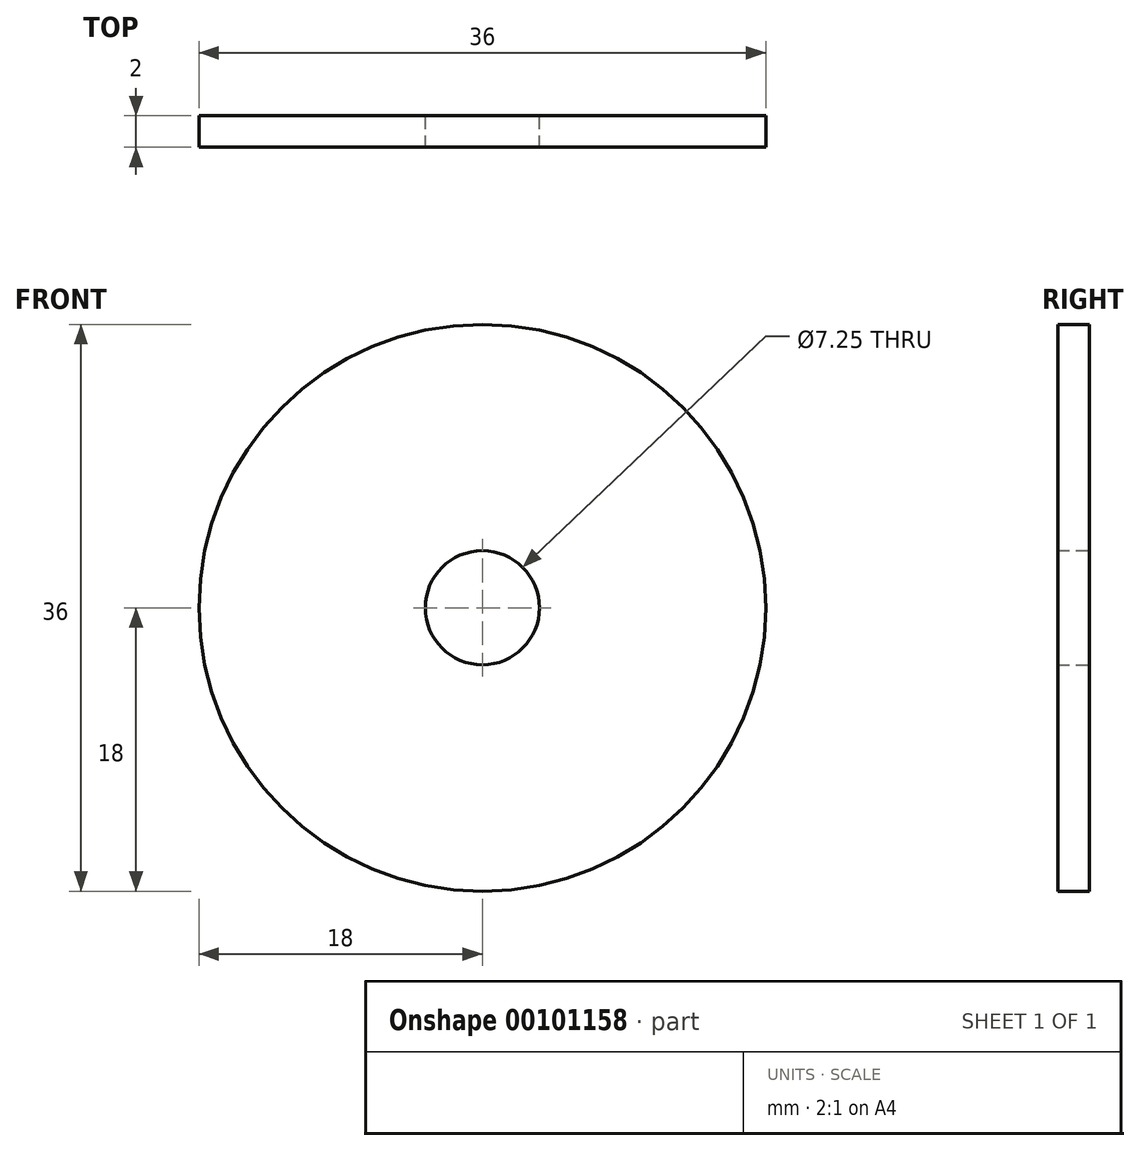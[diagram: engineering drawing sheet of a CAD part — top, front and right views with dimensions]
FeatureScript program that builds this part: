
annotation { "Feature Type Name" : "Feature", "Feature Type Description" : "" }
export const myFeature = defineFeature(function(context is Context, id is Id, definition is map)
    precondition{}
    {
        {
            var Q0;
            Q0=qCreatedBy(makeId("Front.planeOp"),FACE);
            var sketch = newSketch(context, id + "F0", { "sketchPlane" : qUnion([Q0])});
            skCircle(sketch, "E0", {"center": v(0, 0) * mm, "radius": 18 * mm});
            skCircle(sketch, "E1", {"center": v(0, 0) * mm, "radius": 14.5 * mm});
            skCircle(sketch, "E2", {"center": v(0, 0) * mm, "radius": 3.62 * mm});
            skCircle(sketch, "E3", {"center": v(0, 0) * mm, "radius": 6 * mm});
            skLineSegment(sketch, "E4", {"start": v(-2.5, -5.45) * mm, "end": v(-2.5, -14.28) * mm});
            skLineSegment(sketch, "E5.MirrorCS", {"start": v(2.5, -5.45) * mm, "end": v(2.5, -14.28) * mm});
            skLineSegment(sketch, "E6.1.0", {"start": v(5.45, 2.5) * mm, "end": v(14.28, 2.5) * mm});
            skLineSegment(sketch, "E6.1.1", {"start": v(5.45, -2.5) * mm, "end": v(14.28, -2.5) * mm});
            skLineSegment(sketch, "E6.2.0", {"start": v(-2.5, 5.45) * mm, "end": v(-2.5, 14.28) * mm});
            skLineSegment(sketch, "E6.2.1", {"start": v(2.5, 5.45) * mm, "end": v(2.5, 14.28) * mm});
            skLineSegment(sketch, "E6.3.0", {"start": v(-5.45, -2.5) * mm, "end": v(-14.28, -2.5) * mm});
            skLineSegment(sketch, "E6.3.1", {"start": v(-5.45, 2.5) * mm, "end": v(-14.28, 2.5) * mm});
            skSolve(sketch);
        }
        {
            var Q0;
            Q0=makeQuery(id+"F0.imprint","IMPRINT",FACE,{"disambiguationData":[TD([[makeQuery(id+"F0.imprint","IMPRINT",EDGE,{"derivedFrom":sQuery(id+"F0.wireOp",EDGE,"E0")}),1.0]])]});
            var Q1;
            {var subQ0=sQuery(id+"F0.wireOp",EDGE,"E6.3.0");Q1=makeQuery(id+"F0.imprint","IMPRINT",FACE,{"disambiguationData":[TD([[makeQuery(id+"F0.imprint","IMPRINT",EDGE,{"derivedFrom":subQ0}),-1.0]])]});}
            var Q2;
            {var subQ0=sQuery(id+"F0.wireOp",EDGE,"E4");Q2=makeQuery(id+"F0.imprint","IMPRINT",FACE,{"disambiguationData":[TD([[makeQuery(id+"F0.imprint","IMPRINT",EDGE,{"derivedFrom":subQ0}),-1.0]])]});}
            var Q3;
            {var subQ0=sQuery(id+"F0.wireOp",EDGE,"E4");Q3=makeQuery(id+"F0.imprint","IMPRINT",FACE,{"disambiguationData":[TD([[makeQuery(id+"F0.imprint","IMPRINT",EDGE,{"derivedFrom":subQ0}),1.0]])]});}
            var Q4;
            {var subQ0=sQuery(id+"F0.wireOp",EDGE,"E5.MirrorCS");Q4=makeQuery(id+"F0.imprint","IMPRINT",FACE,{"disambiguationData":[TD([[makeQuery(id+"F0.imprint","IMPRINT",EDGE,{"derivedFrom":subQ0}),1.0]])]});}
            var Q5;
            {var subQ0=sQuery(id+"F0.wireOp",EDGE,"E6.1.0");Q5=makeQuery(id+"F0.imprint","IMPRINT",FACE,{"disambiguationData":[TD([[makeQuery(id+"F0.imprint","IMPRINT",EDGE,{"derivedFrom":subQ0}),-1.0]])]});}
            var Q6;
            {var subQ0=sQuery(id+"F0.wireOp",EDGE,"E6.2.0");Q6=makeQuery(id+"F0.imprint","IMPRINT",FACE,{"disambiguationData":[TD([[makeQuery(id+"F0.imprint","IMPRINT",EDGE,{"derivedFrom":subQ0}),-1.0]])]});}
            var Q7;
            {var subQ0=sQuery(id+"F0.wireOp",EDGE,"E6.2.0");Q7=makeQuery(id+"F0.imprint","IMPRINT",FACE,{"disambiguationData":[TD([[makeQuery(id+"F0.imprint","IMPRINT",EDGE,{"derivedFrom":subQ0}),1.0]])]});}
            var Q8;
            Q8=makeQuery(id+"F0.imprint","IMPRINT",FACE,{"disambiguationData":[TD([[makeQuery(id+"F0.imprint","IMPRINT",EDGE,{"derivedFrom":sQuery(id+"F0.wireOp",EDGE,"E2")}),-1.0]])]});
            var Q9;
            {var subQ0=sQuery(id+"F0.wireOp",EDGE,"E6.1.0");Q9=makeQuery(id+"F0.imprint","IMPRINT",FACE,{"disambiguationData":[TD([[makeQuery(id+"F0.imprint","IMPRINT",EDGE,{"derivedFrom":subQ0}),1.0]])]});}
            extrude(context, id + "F1", {"entities" : qUnion([Q0, Q1, Q2, Q3, Q4, Q5, Q6, Q7, Q8, Q9]), "flatOperationType" : FlatOperationType.REMOVE, "depth" : 2 * mm, "offsetDistance" : 25 * mm, "domain" : OperationDomain.MODEL});
        }
    });
